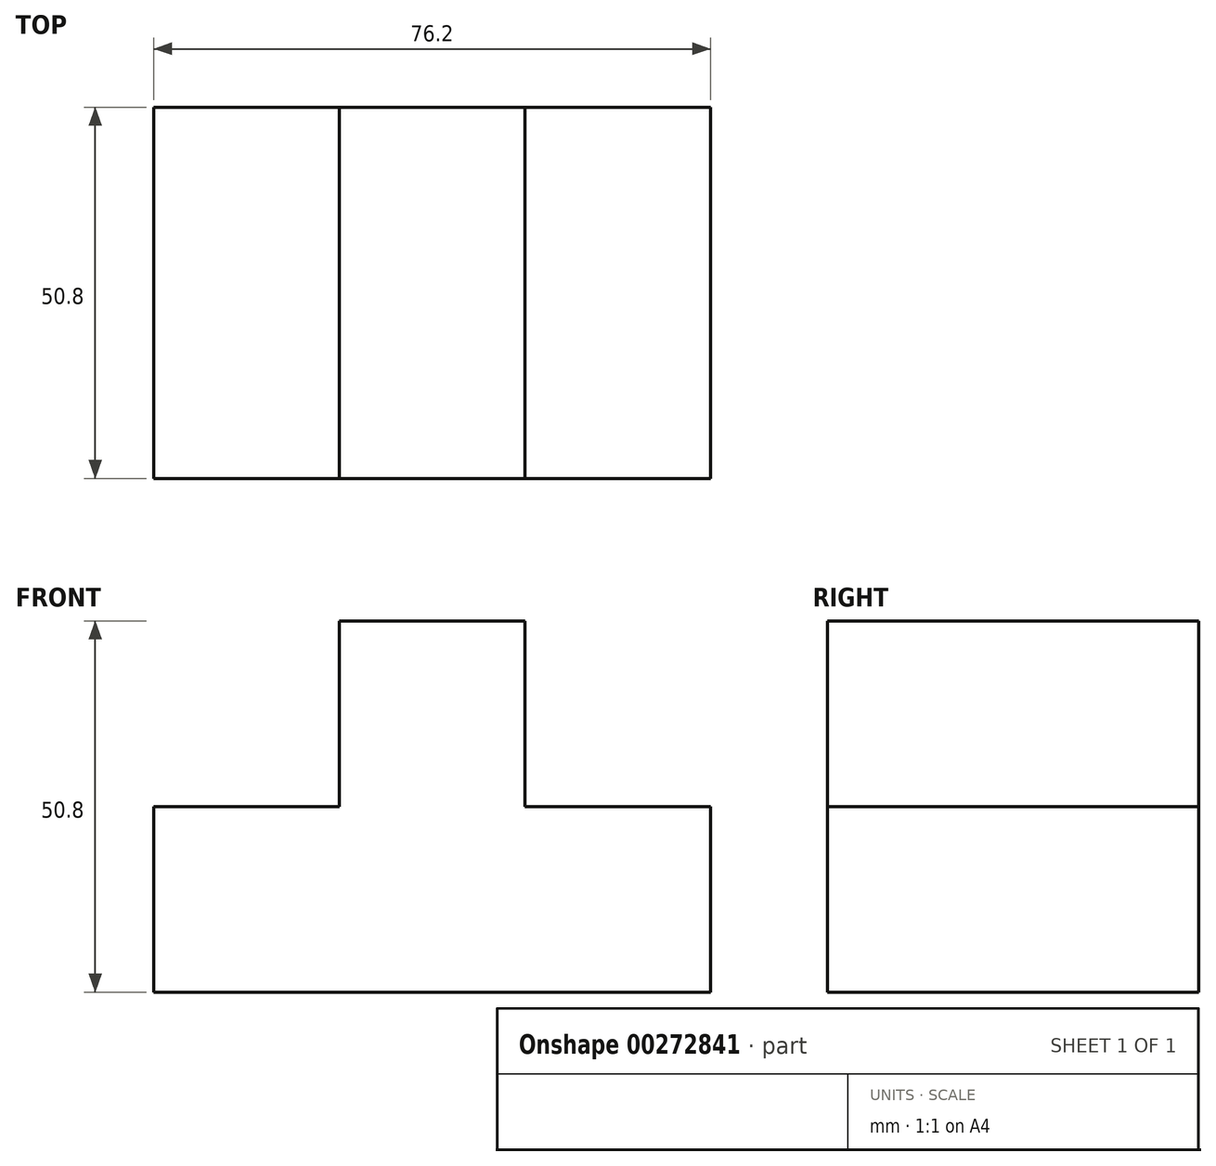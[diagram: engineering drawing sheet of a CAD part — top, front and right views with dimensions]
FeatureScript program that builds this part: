
annotation { "Feature Type Name" : "Feature", "Feature Type Description" : "" }
export const myFeature = defineFeature(function(context is Context, id is Id, definition is map)
    precondition{}
    {
        {
            var Q0;
            Q0=qCreatedBy(makeId("Front.planeOp"),FACE);
            var sketch = newSketch(context, id + "F0", { "sketchPlane" : qUnion([Q0])});
            skLineSegment(sketch, "E0", {"start": v(0, 0) * mm, "end": v(-76.2, 0) * mm});
            skLineSegment(sketch, "E1", {"start": v(0, 0) * mm, "end": v(0, 25.4) * mm});
            skLineSegment(sketch, "E2", {"start": v(0, 25.4) * mm, "end": v(-25.4, 25.4) * mm});
            skLineSegment(sketch, "E3", {"start": v(-25.4, 25.4) * mm, "end": v(-25.4, 50.8) * mm});
            skLineSegment(sketch, "E4", {"start": v(-25.4, 50.8) * mm, "end": v(-50.8, 50.8) * mm});
            skLineSegment(sketch, "E5", {"start": v(-50.8, 50.8) * mm, "end": v(-50.8, 25.4) * mm});
            skLineSegment(sketch, "E6", {"start": v(-50.8, 25.4) * mm, "end": v(-76.2, 25.4) * mm});
            skLineSegment(sketch, "E7", {"start": v(-76.2, 25.4) * mm, "end": v(-76.2, 0) * mm});
            skSolve(sketch);
        }
        {
            var Q0;
            Q0=makeQuery(id+"F0.imprint","IMPRINT",FACE,{"disambiguationData":[TD([[makeQuery(id+"F0.imprint","IMPRINT",EDGE,{"derivedFrom":sQuery(id+"F0.wireOp",EDGE,"E0")}),-1.0]])]});
            extrude(context, id + "F1", {"entities" : qUnion([Q0]), "depth" : 50.8 * mm});
        }
    });
